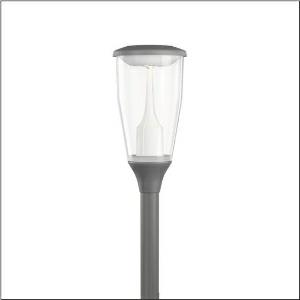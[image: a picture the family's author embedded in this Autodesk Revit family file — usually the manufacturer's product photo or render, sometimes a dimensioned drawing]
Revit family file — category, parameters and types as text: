
# Revit family: dl_11_iq___p1_0a_5xa5565bf14h000022_0962
name_source: partatom
category: Lighting Fixtures
units: mm (PartAtom-declared; Revit-internal decimal feet)

## family parameters
Cut with Voids When Loaded = No
Host = Face
Light Source = No
Part Type = Normal
Room Calculation Point = No
Round Connector Dimension = Use Diameter
Shared = No

## types (1)
- --- (1 x LED, 1530 lm, 12.9 W, 2200K)
    Apparent Load = 13 VA
    CIE Flux Codes = 34 63 91 95 100
    Color Rendering = 70
    Color Temperature = 2200K
    Default Elevation = 1800 mm
    Description = DL 11 iQ, mast luminaire, Module 540 iQ-SR, primary light control with 3 zone facetted reflector, of plastic, silver coated, highly specular, structured, primary optical cover: cover, of PMMA, transparent, light distribution: P1.0a, light emission: direct distribution, primary light characteristic: asymmetric, installation type: post-top, LED, High Power LED, rated luminous flux: 1.560lm, luminous efficacy: 149lm/W, light colour: 722, colour temperature: 2200K, control gear: iQ Street-Remote, control: Street-Remote, Auto-Match, Temp-Guard, Lumen-Switch, Night-Set, Smart-Wire, Light-Fading, Desk-Remote (wireless, voltage-free reading and setting of iQ features in the workshop via application-optimized NFC function/RFID function), optimised constant luminous flux control (CLO 2.0), mains connection: 220..240V, AC, 50/60Hz, connection cable pre-assembled, cable length: 5,5m, start of lifetime: 13W, end of service life: 13W, reduction: 5W, luminaire housing, upper part, of diecast aluminium, coated, SITECO metallic grey (DB 702S), spigot size: 60mm (post-top), mounting height: 3..5m, post-top mast mounting element, of diecast aluminium, coated, SITECO metallic grey (DB 702S), Module 540 iQ-SR, traffic white (RAL 9016), equipment: standard, protection rating (complete): IP66, insulation class (complete): insulation class II (safety insulation), certification: CE, ENEC, ENEC+, VDE, impact resistance: IK07, packaging unit: 1 piece

Light Distribution: P1.0a
    Height = 665 mm
    Lamp = 1 x LED
    Lamp Light Flux = 1530 lm
    Lamp Power = 12.9 W
    Lamp count = 1
    Length = 334 mm
    Luminous efficacy = 119 lm/W
    Manufacturer = Siteco
    ModVariant = No
    Model = 5XA5565BF14H000022
    Number of Poles = 1
    OnlyDefault = Yes
    Power Factor = 1
    Product Name = DL 11 iQ | P1.0a
    Product group = mast luminaire | pylon top
    ProductGroupID = 6100
    Protection Class = Protection class II
    Protection Degree = IP 66
    RLX_Detail_Level = 1
    RLX_Emergency_Light_Flux = 0 lm
    RLX_Emergency_Type = 0
    RLX_Emergency_Type_DB = No
    RlxData = <blob elided: 103969 chars, md5=e5161c3a>
    Socket = socket
    Standby Power = 0 W
    System Light Flux = 1530 lm
    System Power = 13 W
    Type Comments = factory setting: luminous flux: 100 % | dim-lin: 254 | 516 mA
    Type Image = l_1258354.jpg
    URL = http://relux.com
    VarID = @adj_095777
    Voltage = 0 V
    Weight = 0.00 kg
    Width = 0 mm  [stored 0 ft]

note: [stored X ft] marks values corroborated as IEEE doubles in the binary element streams (Revit-internal decimal feet)

## geometry (parser evidence)
native form markers: Blend x4, Sweep x11
no freeform markers — native parametric forms only
